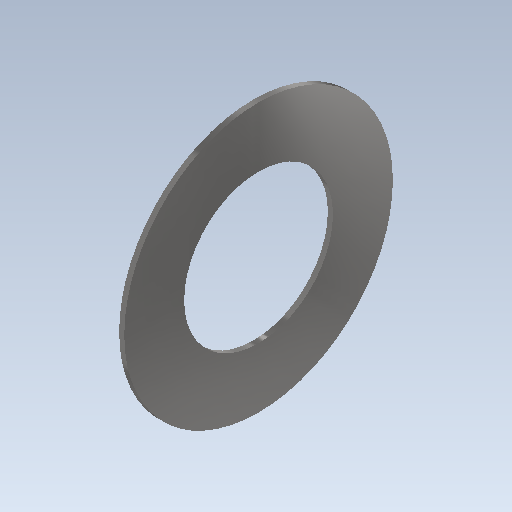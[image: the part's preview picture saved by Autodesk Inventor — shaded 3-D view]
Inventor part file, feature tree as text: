
AUTODESK INVENTOR PART (.ipt)
format: ipt  version: 2020.3 (Build 243373000, 373)  size: 95,744 bytes
history: native  units: mm (DEFAULTED — no unit token found)
features: other x7, revolve x1, sketch x1
ambient origin geometry x8: Origin, YZ Plane, XZ Plane, XY Plane, X Axis, Y Axis, Z Axis, Center Point
bodies: Solid1 (feature_tree)
feature tree (9):
  revolve  "Revolution1"  [1 undecoded]
  other  "ip_st_1_XY"
  other  "ip_st_1_YZ"
  other  "ip_st_1_ZX"
  other  "ip_st_1_X"
  other  "ip_st_1_Y"
  other  "ip_st_1_Z"
  other  "ip_st_1_Center"
  sketch  "Sketch_1"  dims[d0=360.0deg d1=0.0mm]
note: 1 required parameter value undecoded (feature->parameter linkage not recoverable at this tier; creation-order binding heuristic only, values carry confidence <= 0.55)
